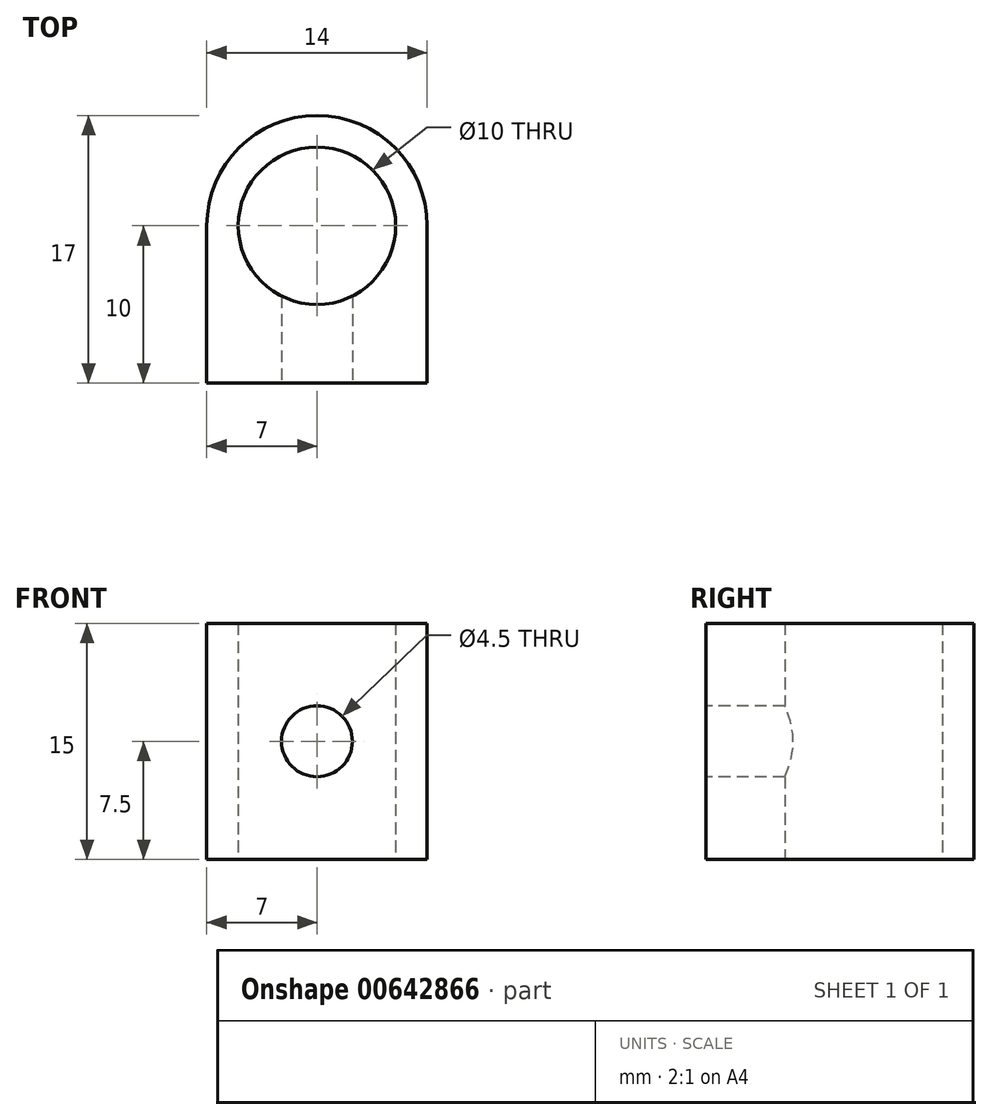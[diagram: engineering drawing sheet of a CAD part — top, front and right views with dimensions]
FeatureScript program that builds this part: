
annotation { "Feature Type Name" : "Feature", "Feature Type Description" : "" }
export const myFeature = defineFeature(function(context is Context, id is Id, definition is map)
    precondition{}
    {
        {
            var Q0;
            Q0=qCreatedBy(makeId("Top.planeOp"),FACE);
            var sketch = newSketch(context, id + "F0", { "sketchPlane" : qUnion([Q0])});
            skLineSegment(sketch, "E0.bottom", {"start": v(-7, 0) * mm, "end": v(7, 0) * mm});
            skLineSegment(sketch, "E0.left", {"start": v(-7, 0) * mm, "end": v(-7, 10) * mm});
            skLineSegment(sketch, "E0.right", {"start": v(7, 0) * mm, "end": v(7, 11.65) * mm});
            skCircle(sketch, "E1", {"center": v(0, 10) * mm, "radius": 7 * mm});
            skCircle(sketch, "E2.0", {"center": v(0, 10) * mm, "radius": 5 * mm});
            skPoint(sketch, "E3", {"position": v(0, 3) * mm});
            skSolve(sketch);
        }
        {
            var Q0;
            Q0=makeQuery(id+"F0.imprint","IMPRINT",FACE,{"disambiguationData":[TD([[makeQuery(id+"F0.imprint","IMPRINT",EDGE,{"derivedFrom":sQuery(id+"F0.wireOp",EDGE,"E2.0")}),-1.0]])]});
            var Q1;
            {var subQ0=sQuery(id+"F0.wireOp",EDGE,"E0.bottom");Q1=makeQuery(id+"F0.imprint","IMPRINT",FACE,{"disambiguationData":[TD([[makeQuery(id+"F0.imprint","IMPRINT",EDGE,{"derivedFrom":subQ0}),1.0]])]});}
            extrude(context, id + "F1", {"entities" : qUnion([Q0, Q1]), "depth" : 15 * mm, "offsetDistance" : 25 * mm});
        }
        {
            var Q0;
            Q0=makeQuery(id+"F1.opExtrude","SWEPT_FACE",FACE,{"disambiguationData":[OSD([sQuery(id+"F0.wireOp",EDGE,"E0.bottom")])]});
            var sketch = newSketch(context, id + "F2", { "sketchPlane" : qUnion([Q0])});
            skCircle(sketch, "E4", {"center": v(0, 7.5) * mm, "radius": 2.25 * mm});
            skLineSegment(sketch, "E5", {"start": v(0, 15) * mm, "end": v(0, 0) * mm, "construction": true});
            skSolve(sketch);
        }
        {
            var Q0;
            Q0=makeQuery(id+"F2.imprint","IMPRINT",FACE,{"disambiguationData":[TD([[makeQuery(id+"F2.imprint","IMPRINT",EDGE,{"derivedFrom":sQuery(id+"F2.wireOp",EDGE,"E4")}),1.0]])]});
            extrude(context, id + "F3", {"entities" : qUnion([Q0]), "operationType" : NewBodyOperationType.REMOVE, "endBound" : BoundingType.UP_TO_NEXT, "oppositeDirection" : true, "depth" : 25 * mm, "offsetDistance" : 25 * mm});
        }
    });
